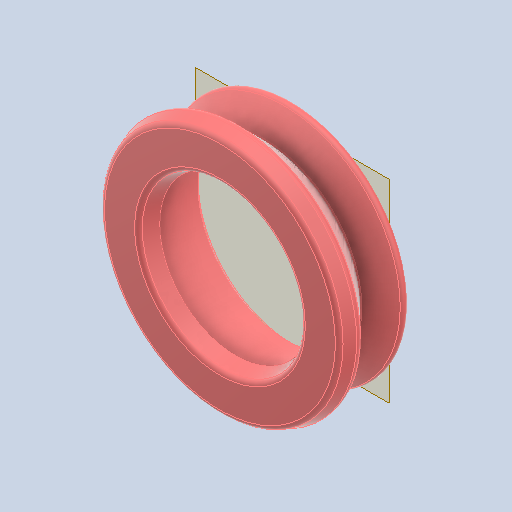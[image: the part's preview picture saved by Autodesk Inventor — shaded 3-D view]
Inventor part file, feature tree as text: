
AUTODESK INVENTOR PART (.ipt)
format: ipt  version: 2022 (Build 260153000, 153)  size: 211,456 bytes
history: native  units: in
note: dims shown in document units (in); Inventor stores cm internally (conversion verified against a paired STEP export)
features: other x3, sketch x1, plane x1
ambient origin geometry x8: Origin, YZ Plane, XZ Plane, XY Plane, X Axis, Y Axis, Z Axis, Center Point
bodies: Solid1 (feature_tree)
feature tree (5):
  other  "vroller.ipt"
  other  "Solid1::vroller.ipt"
  other  "TaggingFeature1"
  sketch  "Sketch1"  dims[d0=0.3937in]
  plane  "Work Plane1"
